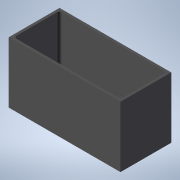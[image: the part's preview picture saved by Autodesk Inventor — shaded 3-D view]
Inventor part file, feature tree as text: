
AUTODESK INVENTOR PART (.ipt)
format: ipt  version: 2020 (Build 240168000, 168)  size: 111,616 bytes
history: native  units: mm
features: extrude x2, sketch x2
ambient origin geometry x8: Origin, YZ Plane, XZ Plane, XY Plane, X Axis, Y Axis, Z Axis, Center Point
bodies: Solid1 (feature_tree)
feature tree (4):
  extrude  "Extrusion1"  Depth=100.0mm
  extrude  "Extrusion2"  Depth=5.0mm
  sketch  "Sketch1"  dims[d0=220.0mm d1=100.0mm]
  sketch  "Sketch2"  dims[d2=120.0mm d3=0.0mm d4=5.0mm d5=5.0mm d6=5.0mm d7=5.0mm d8=5.0mm d9=115.0mm d10=0.0mm]
